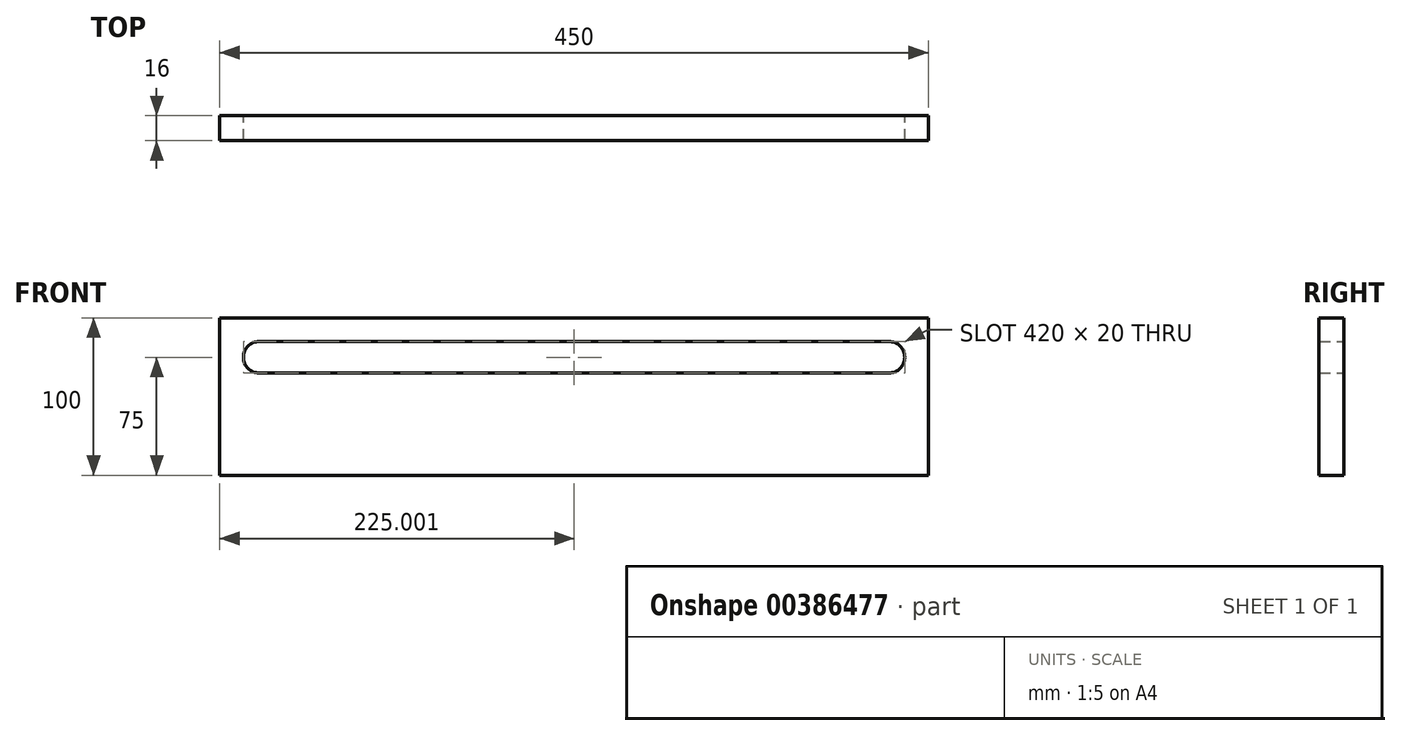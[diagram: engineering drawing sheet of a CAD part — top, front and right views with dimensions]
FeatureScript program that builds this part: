
annotation { "Feature Type Name" : "Feature", "Feature Type Description" : "" }
export const myFeature = defineFeature(function(context is Context, id is Id, definition is map)
    precondition{}
    {
        {
            var Q0;
            Q0=qCreatedBy(makeId("Front.planeOp"),FACE);
            var sketch = newSketch(context, id + "F0", { "sketchPlane" : qUnion([Q0])});
            skLineSegment(sketch, "E0.bottom", {"start": v(-238.26, 42.48) * mm, "end": v(211.74, 42.48) * mm});
            skLineSegment(sketch, "E0.top", {"start": v(-238.26, -57.52) * mm, "end": v(211.74, -57.52) * mm});
            skLineSegment(sketch, "E0.left", {"start": v(-238.26, 42.48) * mm, "end": v(-238.26, -57.52) * mm});
            skLineSegment(sketch, "E0.right", {"start": v(211.74, 42.48) * mm, "end": v(211.74, -57.52) * mm});
            skLineSegment(sketch, "E1.bottom", {"start": v(-213.26, 27.48) * mm, "end": v(186.74, 27.48) * mm});
            skLineSegment(sketch, "E1.top", {"start": v(-213.26, 7.48) * mm, "end": v(186.74, 7.48) * mm});
            skLineSegment(sketch, "E1.left", {"start": v(-213.26, 27.48) * mm, "end": v(-213.26, 7.48) * mm});
            skLineSegment(sketch, "E1.right", {"start": v(186.74, 27.48) * mm, "end": v(186.74, 7.48) * mm});
            skArc(sketch, "E2", {"start": v(-213.26, 27.48) * mm, "mid": v(-223.26, 17.48) * mm, "end": v(-213.26, 7.48) * mm});
            skArc(sketch, "E3", {"start": v(186.74, 27.48) * mm, "mid": v(196.74, 17.48) * mm, "end": v(186.74, 7.48) * mm});
            skSolve(sketch);
        }
        {
            var Q0;
            Q0=makeQuery(id+"F0.imprint","IMPRINT",FACE,{"disambiguationData":[TD([[makeQuery(id+"F0.imprint","IMPRINT",EDGE,{"derivedFrom":sQuery(id+"F0.wireOp",EDGE,"E0.bottom")}),-1.0]])]});
            extrude(context, id + "F1", {"entities" : qUnion([Q0]), "depth" : 16 * mm});
        }
    });
